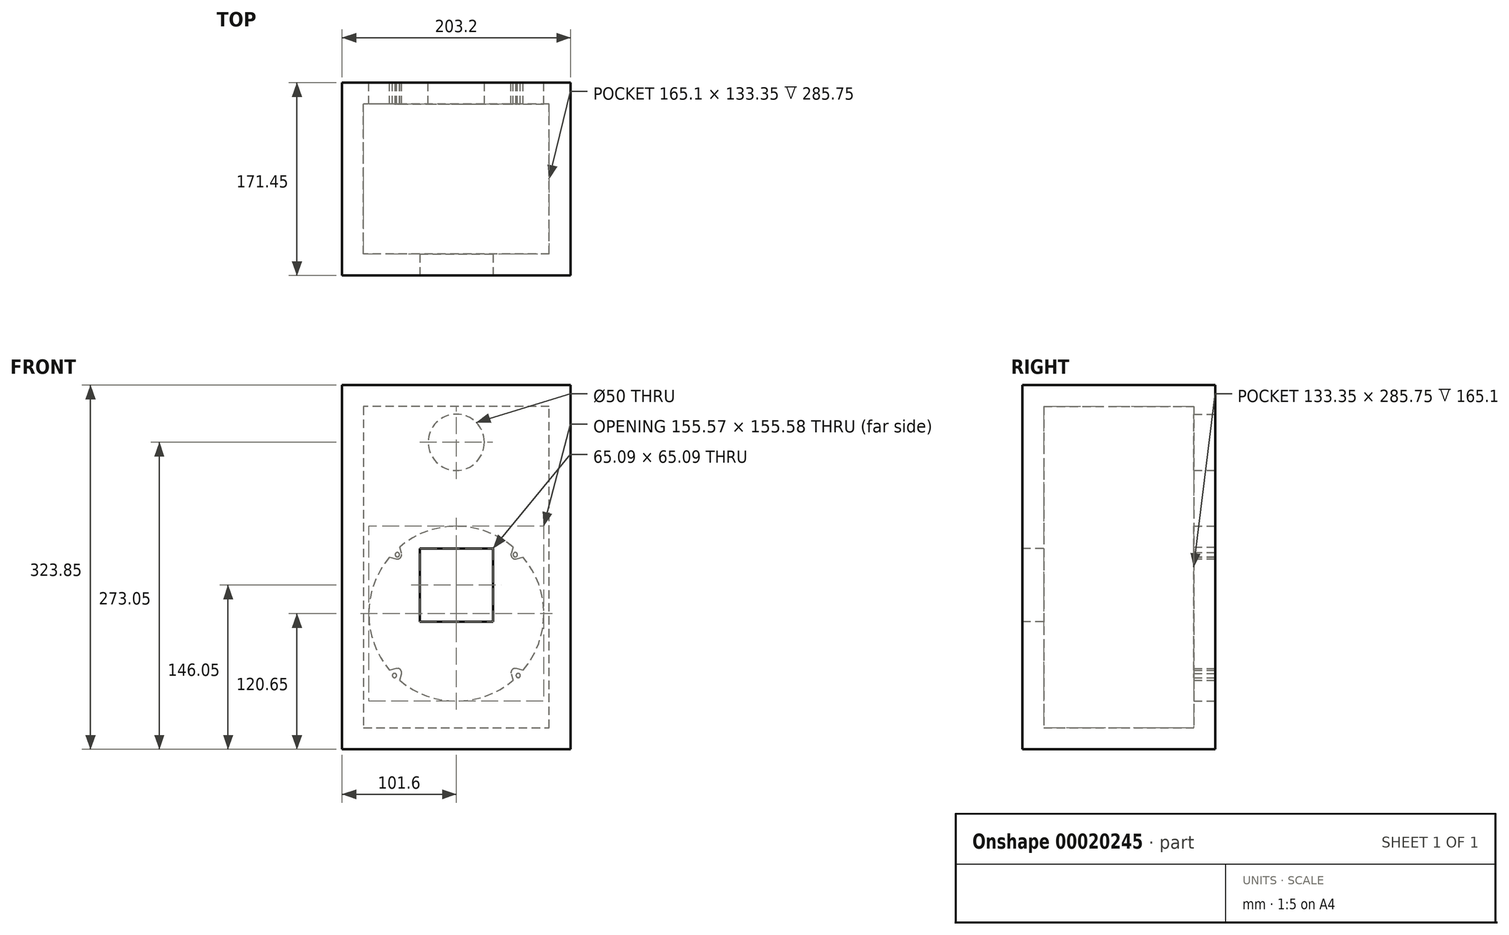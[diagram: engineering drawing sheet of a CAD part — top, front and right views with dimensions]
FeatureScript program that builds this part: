
annotation { "Feature Type Name" : "Feature", "Feature Type Description" : "" }
export const myFeature = defineFeature(function(context is Context, id is Id, definition is map)
    precondition{}
    {
        {
            var Q0;
            Q0=qCreatedBy(makeId("Front.planeOp"),FACE);
            var sketch = newSketch(context, id + "F0", { "sketchPlane" : qUnion([Q0])});
            skLineSegment(sketch, "E0.rect.top", {"start": v(101.6, 127) * mm, "end": v(-101.6, 127) * mm});
            skLineSegment(sketch, "E0.rect.left", {"start": v(101.6, -127) * mm, "end": v(101.6, 127) * mm});
            skLineSegment(sketch, "E0.rect.right", {"start": v(-101.6, -127) * mm, "end": v(-101.6, 127) * mm});
            skPoint(sketch, "E0.rect.middle", {"position": v(0, 0) * mm});
            skCircle(sketch, "E1", {"center": v(0, -76.2) * mm, "radius": 82.55 * mm});
            skLineSegment(sketch, "E2", {"start": v(0, -158.75) * mm, "end": v(0, 6.35) * mm, "construction": true});
            skLineSegment(sketch, "E3", {"start": v(-82.55, -76.2) * mm, "end": v(82.55, -76.2) * mm, "construction": true});
            skPoint(sketch, "E4", {"position": v(-55, -21.2) * mm});
            skLineSegment(sketch, "E5", {"start": v(-55, -21.2) * mm, "end": v(0, -76.2) * mm, "construction": true});
            skLineSegment(sketch, "E6", {"start": v(-55, -21.2) * mm, "end": v(-55, -76.2) * mm, "construction": true});
            skLineSegment(sketch, "E7", {"start": v(-55, -21.2) * mm, "end": v(0, -21.2) * mm, "construction": true});
            skCircle(sketch, "E8", {"center": v(0, -76.2) * mm, "radius": 77.79 * mm});
            skPoint(sketch, "E9.MirrorP", {"position": v(55, -21.2) * mm});
            skPoint(sketch, "E10.MirrorP", {"position": v(55, -131.2) * mm});
            skPoint(sketch, "E11.MirrorP", {"position": v(-55, -131.2) * mm});
            skLineSegment(sketch, "E12", {"start": v(-59.31, -25.87) * mm, "end": v(-53.42, -27.45) * mm});
            skLineSegment(sketch, "E13", {"start": v(-48.75, -22.78) * mm, "end": v(-50.33, -16.89) * mm});
            skPoint(sketch, "E14.visualSharp", {"position": v(-47.04, -29.16) * mm});
            skArc(sketch, "E14.filletArc", {"start": v(-53.42, -27.45) * mm, "mid": v(-49.74, -26.46) * mm, "end": v(-48.75, -22.78) * mm});
            skLineSegment(sketch, "E15.1.0", {"start": v(-50.33, -135.51) * mm, "end": v(-48.75, -129.62) * mm});
            skArc(sketch, "E15.1.1", {"start": v(-48.75, -129.62) * mm, "mid": v(-49.74, -125.94) * mm, "end": v(-53.42, -124.95) * mm});
            skLineSegment(sketch, "E15.1.2", {"start": v(-53.42, -124.95) * mm, "end": v(-59.31, -126.53) * mm});
            skLineSegment(sketch, "E15.2.0", {"start": v(59.31, -126.53) * mm, "end": v(53.42, -124.95) * mm});
            skArc(sketch, "E15.2.1", {"start": v(53.42, -124.95) * mm, "mid": v(49.74, -125.94) * mm, "end": v(48.75, -129.62) * mm});
            skLineSegment(sketch, "E15.2.2", {"start": v(48.75, -129.62) * mm, "end": v(50.33, -135.51) * mm});
            skLineSegment(sketch, "E15.3.0", {"start": v(50.33, -16.89) * mm, "end": v(48.75, -22.78) * mm});
            skArc(sketch, "E15.3.1", {"start": v(48.75, -22.78) * mm, "mid": v(49.74, -26.46) * mm, "end": v(53.42, -27.45) * mm});
            skLineSegment(sketch, "E15.3.2", {"start": v(53.42, -27.45) * mm, "end": v(59.31, -25.87) * mm});
            skCircle(sketch, "E16", {"center": v(0, 76.2) * mm, "radius": 25 * mm});
            skCircle(sketch, "E17", {"center": v(0, 76.2) * mm, "radius": 19 * mm});
            skCircle(sketch, "E18", {"center": v(0, 76.2) * mm, "radius": 16.25 * mm});
            skCircle(sketch, "E19", {"center": v(0, 76.2) * mm, "radius": 20.63 * mm});
            skLineSegment(sketch, "E20", {"start": v(101.6, -127) * mm, "end": v(101.6, -196.85) * mm});
            skLineSegment(sketch, "E21", {"start": v(101.6, -196.85) * mm, "end": v(-101.6, -196.85) * mm});
            skLineSegment(sketch, "E22", {"start": v(-101.6, -196.85) * mm, "end": v(-101.6, -127) * mm});
            skSolve(sketch);
        }
        {
            var Q0;
            Q0=makeQuery(id+"F0.imprint","IMPRINT",FACE,{"disambiguationData":[TD([[makeQuery(id+"F0.imprint","IMPRINT",EDGE,{"derivedFrom":sQuery(id+"F0.wireOp",EDGE,"E0.rect.top")}),1.0]])]});
            var Q1;
            Q1=makeQuery(id+"F0.imprint","IMPRINT",FACE,{"disambiguationData":[TD([[makeQuery(id+"F0.imprint","IMPRINT",EDGE,{"derivedFrom":sQuery(id+"F0.wireOp",EDGE,"E1")}),1.0]])]});
            var Q2;
            {var subQ1=sQuery(id+"F0.wireOp",EDGE,"E15.1.0");Q2=makeQuery(id+"F0.imprint","IMPRINT",FACE,{"disambiguationData":[TD([[makeQuery(id+"F0.imprint","IMPRINT",EDGE,{"derivedFrom":subQ1}),1.0]])]});}
            var Q3;
            {var subQ1=sQuery(id+"F0.wireOp",EDGE,"E15.2.0");Q3=makeQuery(id+"F0.imprint","IMPRINT",FACE,{"disambiguationData":[TD([[makeQuery(id+"F0.imprint","IMPRINT",EDGE,{"derivedFrom":subQ1}),1.0]])]});}
            var Q4;
            {var subQ1=sQuery(id+"F0.wireOp",EDGE,"E15.3.0");Q4=makeQuery(id+"F0.imprint","IMPRINT",FACE,{"disambiguationData":[TD([[makeQuery(id+"F0.imprint","IMPRINT",EDGE,{"derivedFrom":subQ1}),1.0]])]});}
            var Q5;
            {var subQ1=sQuery(id+"F0.wireOp",EDGE,"E12");Q5=makeQuery(id+"F0.imprint","IMPRINT",FACE,{"disambiguationData":[TD([[makeQuery(id+"F0.imprint","IMPRINT",EDGE,{"derivedFrom":subQ1}),1.0]])]});}
            extrude(context, id + "F1", {"entities" : qUnion([Q0, Q1, Q2, Q3, Q4, Q5]), "depth" : 19.05 * mm});
        }
        {
            var Q0;
            {var subQ1=sQuery(id+"F0.wireOp",EDGE,"E15.3.0");Q0=makeQuery(id+"F0.imprint","IMPRINT",FACE,{"disambiguationData":[TD([[makeQuery(id+"F0.imprint","IMPRINT",EDGE,{"derivedFrom":subQ1}),1.0]])]});}
            var Q1;
            {var subQ1=sQuery(id+"F0.wireOp",EDGE,"E15.2.0");Q1=makeQuery(id+"F0.imprint","IMPRINT",FACE,{"disambiguationData":[TD([[makeQuery(id+"F0.imprint","IMPRINT",EDGE,{"derivedFrom":subQ1}),1.0]])]});}
            var Q2;
            {var subQ1=sQuery(id+"F0.wireOp",EDGE,"E15.1.0");Q2=makeQuery(id+"F0.imprint","IMPRINT",FACE,{"disambiguationData":[TD([[makeQuery(id+"F0.imprint","IMPRINT",EDGE,{"derivedFrom":subQ1}),1.0]])]});}
            var Q3;
            {var subQ1=sQuery(id+"F0.wireOp",EDGE,"E12");Q3=makeQuery(id+"F0.imprint","IMPRINT",FACE,{"disambiguationData":[TD([[makeQuery(id+"F0.imprint","IMPRINT",EDGE,{"derivedFrom":subQ1}),1.0]])]});}
            extrude(context, id + "F2", {"entities" : qUnion([Q0, Q1, Q2, Q3]), "operationType" : NewBodyOperationType.ADD, "depth" : 6.35 * mm});
        }
        {
            var Q0;
            Q0=sQuery(id+"F0.wireOp",VERTEX,"E15.3.1.center");
            var Q1;
            Q1=sQuery(id+"F0.wireOp",VERTEX,"E14.filletArc.center");
            var Q2;
            Q2=sQuery(id+"F0.wireOp",VERTEX,"E11.MirrorP");
            var Q3;
            Q3=sQuery(id+"F0.wireOp",VERTEX,"E10.MirrorP");
            var Q4;
            Q4=makeQuery(id+"F1.opExtrude","SWEPT_BODY",BODY,{"disambiguationData":[OSD([sQuery(id+"F0.wireOp",EDGE,"E0.rect.bottom"),sQuery(id+"F0.wireOp",EDGE,"E0.rect.top"),sQuery(id+"F0.wireOp",EDGE,"E0.rect.left"),sQuery(id+"F0.wireOp",EDGE,"E0.rect.right"),sQuery(id+"F0.wireOp",EDGE,"E8")])]});
            hole(context, id + "F3", {"style" : HoleStyle.SIMPLE, "holeDiameter" : 3.8 * mm, "endStyle" : HoleEndStyle.THROUGH, "oppositeDirection" : true, "locations" : qUnion([Q0, Q1, Q2, Q3]), "scope" : qUnion([Q4])});
        }
        {
            var Q0;
            Q0=makeQuery(id+"F1.opExtrude","CAP_FACE",FACE,{"disambiguationData":[OSD([sQuery(id+"F0.wireOp",EDGE,"E0.rect.top"),sQuery(id+"F0.wireOp",EDGE,"E0.rect.left"),sQuery(id+"F0.wireOp",EDGE,"E0.rect.right"),sQuery(id+"F0.wireOp",EDGE,"E8"),sQuery(id+"F0.wireOp",EDGE,"E12"),sQuery(id+"F0.wireOp",EDGE,"E13"),sQuery(id+"F0.wireOp",EDGE,"E14.filletArc"),sQuery(id+"F0.wireOp",EDGE,"E15.1.0"),sQuery(id+"F0.wireOp",EDGE,"E15.1.1"),sQuery(id+"F0.wireOp",EDGE,"E15.1.2"),sQuery(id+"F0.wireOp",EDGE,"E15.2.0"),sQuery(id+"F0.wireOp",EDGE,"E15.2.1"),sQuery(id+"F0.wireOp",EDGE,"E15.2.2"),sQuery(id+"F0.wireOp",EDGE,"E15.3.0"),sQuery(id+"F0.wireOp",EDGE,"E15.3.1"),sQuery(id+"F0.wireOp",EDGE,"E15.3.2"),sQuery(id+"F0.wireOp",EDGE,"E16"),sQuery(id+"F0.wireOp",EDGE,"E20"),sQuery(id+"F0.wireOp",EDGE,"E21"),sQuery(id+"F0.wireOp",EDGE,"E22")])],"isStart":false});
            var sketch = newSketch(context, id + "F4", { "sketchPlane" : qUnion([Q0])});
            skLineSegment(sketch, "E23.0.0", {"start": v(101.6, -196.85) * mm, "end": v(101.6, 127) * mm});
            skLineSegment(sketch, "E23.0.1", {"start": v(101.6, 127) * mm, "end": v(-101.6, 127) * mm});
            skLineSegment(sketch, "E23.0.2", {"start": v(-101.6, 127) * mm, "end": v(-101.6, -196.85) * mm});
            skLineSegment(sketch, "E23.0.3", {"start": v(-101.6, -196.85) * mm, "end": v(101.6, -196.85) * mm});
            skLineSegment(sketch, "E24.0", {"start": v(-82.55, 107.95) * mm, "end": v(-82.55, -177.8) * mm});
            skLineSegment(sketch, "E24.1", {"start": v(82.55, 107.95) * mm, "end": v(-82.55, 107.95) * mm});
            skLineSegment(sketch, "E24.2", {"start": v(82.55, -177.8) * mm, "end": v(82.55, 107.95) * mm});
            skLineSegment(sketch, "E24.3", {"start": v(-82.55, -177.8) * mm, "end": v(82.55, -177.8) * mm});
            skSolve(sketch);
        }
        {
            var Q0;
            Q0 = qSketchRegion(id + "F4", true);
            extrude(context, id + "F5", {"entities" : qUnion([Q0]), "operationType" : NewBodyOperationType.ADD, "depth" : 152.4 * mm});
        }
        {
            var Q0;
            Q0=makeQuery(id+"F5.opExtrude","CAP_FACE",FACE,{"disambiguationData":[OSD([sQuery(id+"F4.wireOp",EDGE,"E23.0.0"),sQuery(id+"F4.wireOp",EDGE,"E23.0.1"),sQuery(id+"F4.wireOp",EDGE,"E23.0.2"),sQuery(id+"F4.wireOp",EDGE,"E23.0.3"),sQuery(id+"F4.wireOp",EDGE,"E24.0"),sQuery(id+"F4.wireOp",EDGE,"E24.1"),sQuery(id+"F4.wireOp",EDGE,"E24.2"),sQuery(id+"F4.wireOp",EDGE,"E24.3")])],"isStart":false});
            var sketch = newSketch(context, id + "F6", { "sketchPlane" : qUnion([Q0])});
            skLineSegment(sketch, "E25.0", {"start": v(-101.6, -127) * mm, "end": v(-101.6, 127) * mm});
            skLineSegment(sketch, "E26.0", {"start": v(101.6, 127) * mm, "end": v(-101.6, 127) * mm});
            skLineSegment(sketch, "E27.0", {"start": v(101.6, -196.85) * mm, "end": v(-101.6, -196.85) * mm});
            skLineSegment(sketch, "E28.0", {"start": v(101.6, -127) * mm, "end": v(101.6, -196.85) * mm});
            skLineSegment(sketch, "E29.0", {"start": v(101.6, -127) * mm, "end": v(101.6, 127) * mm});
            skLineSegment(sketch, "E30.0", {"start": v(-101.6, -196.85) * mm, "end": v(-101.6, -127) * mm});
            skSolve(sketch);
        }
        {
            var Q0;
            Q0 = qSketchRegion(id + "F6", true);
            extrude(context, id + "F7", {"entities" : qUnion([Q0]), "operationType" : NewBodyOperationType.ADD, "oppositeDirection" : true, "depth" : 19.05 * mm});
        }
        {
            var Q0;
            Q0=makeQuery(id+"F7.boolean.opBoolean","MERGE",FACE,{"derivedFrom":[makeQuery(id+"F5.opExtrude","CAP_FACE",FACE,{"disambiguationData":[OSD([sQuery(id+"F4.wireOp",EDGE,"E23.0.0"),sQuery(id+"F4.wireOp",EDGE,"E23.0.1"),sQuery(id+"F4.wireOp",EDGE,"E23.0.2"),sQuery(id+"F4.wireOp",EDGE,"E23.0.3"),sQuery(id+"F4.wireOp",EDGE,"E24.0"),sQuery(id+"F4.wireOp",EDGE,"E24.1"),sQuery(id+"F4.wireOp",EDGE,"E24.2"),sQuery(id+"F4.wireOp",EDGE,"E24.3")])],"isStart":false}),makeQuery(id+"F7.opExtrude","CAP_FACE",FACE,{"disambiguationData":[OSD([sQuery(id+"F6.wireOp",EDGE,"E25.0"),sQuery(id+"F6.wireOp",EDGE,"E26.0"),sQuery(id+"F6.wireOp",EDGE,"E27.0"),sQuery(id+"F6.wireOp",EDGE,"E28.0"),sQuery(id+"F6.wireOp",EDGE,"E29.0"),sQuery(id+"F6.wireOp",EDGE,"E30.0")])],"isStart":true})]});
            var sketch = newSketch(context, id + "F8", { "sketchPlane" : qUnion([Q0])});
            skLineSegment(sketch, "E31.rect.bottom", {"start": v(32.54, -83.34) * mm, "end": v(-32.54, -83.34) * mm});
            skLineSegment(sketch, "E31.rect.top", {"start": v(32.54, -18.26) * mm, "end": v(-32.54, -18.26) * mm});
            skLineSegment(sketch, "E31.rect.left", {"start": v(32.54, -83.34) * mm, "end": v(32.54, -18.26) * mm});
            skLineSegment(sketch, "E31.rect.right", {"start": v(-32.54, -83.34) * mm, "end": v(-32.54, -18.26) * mm});
            skPoint(sketch, "E31.rect.middle", {"position": v(0, -50.8) * mm});
            skSolve(sketch);
        }
        {
            var Q0;
            Q0 = qSketchRegion(id + "F8", true);
            var Q1;
            Q1=makeQuery(id+"F7.opExtrude","CAP_FACE",FACE,{"disambiguationData":[OSD([sQuery(id+"F6.wireOp",EDGE,"E25.0"),sQuery(id+"F6.wireOp",EDGE,"E26.0"),sQuery(id+"F6.wireOp",EDGE,"E27.0"),sQuery(id+"F6.wireOp",EDGE,"E28.0"),sQuery(id+"F6.wireOp",EDGE,"E29.0"),sQuery(id+"F6.wireOp",EDGE,"E30.0")])],"isStart":false});
            extrude(context, id + "F9", {"entities" : qUnion([Q0]), "operationType" : NewBodyOperationType.REMOVE, "endBound" : BoundingType.UP_TO_SURFACE, "oppositeDirection" : true, "endBoundEntityFace" : qUnion([Q1]), "depth" : 25.4 * mm});
        }
    });
